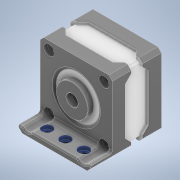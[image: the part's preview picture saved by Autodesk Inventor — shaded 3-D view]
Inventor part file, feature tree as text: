
AUTODESK INVENTOR PART (.ipt)
format: ipt  version: 2021 (Build 250183000, 183)  size: 523,264 bytes
history: native  units: mm
features: sketch x14, projected_geometry x12, extrude x11, fillet x4, mirror x4, reference x4, hole x3, other x2
ambient origin geometry x8: Origin, YZ Plane, XZ Plane, XY Plane, X Axis, Y Axis, Z Axis, Center Point
bodies: Solid1 (feature_tree)
feature tree (54):
  extrude  "Extrusion1"  Depth=50.0mm
  hole  "Hole1"  [1 undecoded]
  extrude  "Extrusion2"  Depth=2.5mm
  fillet  "Fillet1"  Radius=2.5mm
  extrude  "Extrusion3"  Depth=2.5mm
  fillet  "Fillet2"  Radius=34.0mm
  extrude  "Extrusion6"  Depth=31.0mm
  extrude  "Extrusion7"  Depth=15.5mm
  extrude  "Extrusion8"  Depth=2.0mm
  mirror  "Mirror1"
  extrude  "Extrusion9"  Depth=2.0mm
  mirror  "Mirror2"
  mirror  "Mirror3"
  mirror  "Mirror4"
  extrude  "Extrusion12"  Depth=8.0mm
  extrude  "Extrusion11"  Depth=4.0mm
  extrude  "Extrusion10"  Depth=8.0mm
  hole  "Hole5"  [1 undecoded]
  hole  "Hole4"  [1 undecoded]
  extrude  "Extrusion14"  Depth=2.0mm TaperAngle=0.0deg
  fillet  "Fillet4"  Radius=8.0mm
  fillet  "Fillet5"  Radius=4.0mm
  sketch  "Sketch1"  dims[d0=50.0mm d1=2.5mm]
  sketch  "Sketch2"  dims[d2=2.5mm d3=2.5mm]
  projected_geometry  "Projected Loop1"
  sketch  "Sketch3"  dims[d4=2.5mm d5=2.5mm d6=2.5mm]
  sketch  "Sketch4"  dims[d7=2.5mm d8=2.5mm d9=34.0mm d10=0.0mm]
  projected_geometry  "Projected Loop2"
  sketch  "Sketch7"  dims[d11=31.0mm d12=31.0mm]
  projected_geometry  "Projected Loop4"
  sketch  "Sketch8"  dims[d13=15.5mm d14=15.5mm]
  projected_geometry  "Projected Loop5"
  projected_geometry  "Projected Loop6"
  projected_geometry  "Projected Loop7"
  sketch  "Sketch9"  dims[d15=3.458734mm d16=8.0mm d17=4.5mm d18=2.0mm d19=90.0deg d20=10.8mm d21=20.594885mm d22=30.0mm]
  projected_geometry  "Projected Loop8"
  projected_geometry  "Projected Loop9"
  projected_geometry  "Projected Loop10"
  sketch  "Sketch10"  dims[d23=1.0mm d24=0.0mm d25=2.0mm]
  projected_geometry  "Projected Loop11"
  sketch  "Sketch11"  dims[d26=22.0mm d27=8.0mm]
  sketch  "Sketch13"  dims[d28=4.0mm d29=0.0mm d33=0.25mm]
  sketch  "Sketch17"  dims[d37=17.0mm d38=8.0mm]
  sketch  "Sketch18"  dims[d39=4.0mm d40=2.0mm]
  reference  "Reference3"
  reference  "Reference4"
  reference  "Reference5"
  reference  "Reference6"
  sketch  "Sketch20"  dims[d41=2.0mm d42=2.0mm d43=0.0mm]
  sketch  "Sketch21"  dims[d44=2.0mm d45=0.0mm d46=2.0mm d47=0.0mm d48=8.0mm d49=4.0mm d50=4.0mm d51=2.0mm d52=2.0mm d53=0.0mm d55=15.0mm d56=0.0mm d72=6.0mm d73=0.0mm d75=5.0mm d83=5.0mm d84=5.0mm d85=5.0mm d86=5.0mm d87=10.0mm d88=0.0mm d89=4.0mm d90=8.0mm d91=7.25mm d92=2.8mm d93=90.0deg d94=8.0mm d95=20.594885mm d99=4.0mm d111=12.7mm d112=12.7mm d114=50.0mm d115=25.0mm d116=15.0mm d117=7.5mm d118=4.0mm d119=6.0mm d120=7.25mm d121=2.8mm d122=90.0deg d123=8.0mm d124=20.594885mm d125=0.0mm d126=0.0mm d130=2.0mm d131=1.0mm]
  projected_geometry  "Projected Loop13"
  projected_geometry  "Projected Loop14"
  other  "Mounting Platform.iam"
  other  "Mounting plate:1"
note: 3 required parameter values undecoded (feature->parameter linkage not recoverable at this tier; creation-order binding heuristic only, values carry confidence <= 0.55)
